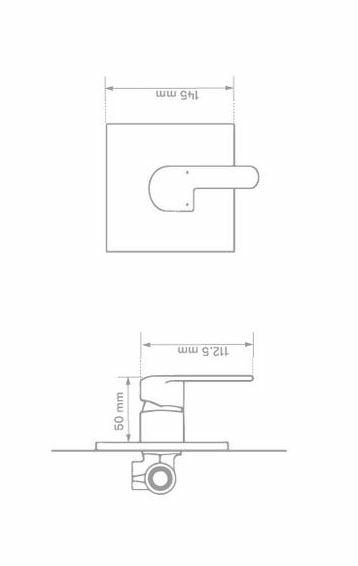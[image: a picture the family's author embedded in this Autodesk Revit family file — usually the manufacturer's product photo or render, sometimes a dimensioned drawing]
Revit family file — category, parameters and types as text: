
# Revit family: 01-2209-11 MONOMANDO LAVAPLATOS COLECCIÓN TIFFANY
name_source: partatom
category: Plumbing Fixtures
revit_build: Autodesk Revit 2018 (Build: 20170223_1515(x64)
units: mm (PartAtom-declared; Revit-internal decimal feet)

## family parameters
Cut with Voids When Loaded = No
Host = Face
OmniClass Number = 23.31.11.00
Part Type = Normal
Room Calculation Point = No
Round Connector Dimension = Use Diameter
Shared = No

## types (1)
- 01-2209-11
    Alto = 340 mm
    Alto difusor = 220 mm
    Brazo y cuerpo = Metal Laton Cromado
    CW Connection = Yes
    Default Elevation = 0 mm  [stored 0 ft]
    Description = MONOMANDO
    HW Connection = Yes
    Link Ficha Tecnica = http://infotecnica.gricol.com
    Manija y base = Metal Zamak Cromado
    Manufacturer = Gricol
    Model = 01-2209-11
    Product Name = MONOMANDO LAVAPLATOS COLECCIÓN TIFFANY
    Type Image = <None>
    URL = https://www.gricol.com
    Vent Connection = No
    Waste Connection = No

note: [stored X ft] marks values corroborated as IEEE doubles in the binary element streams (Revit-internal decimal feet)

## geometry (parser evidence)
native form markers: Blend x2, Sweep x3
no freeform markers — native parametric forms only
